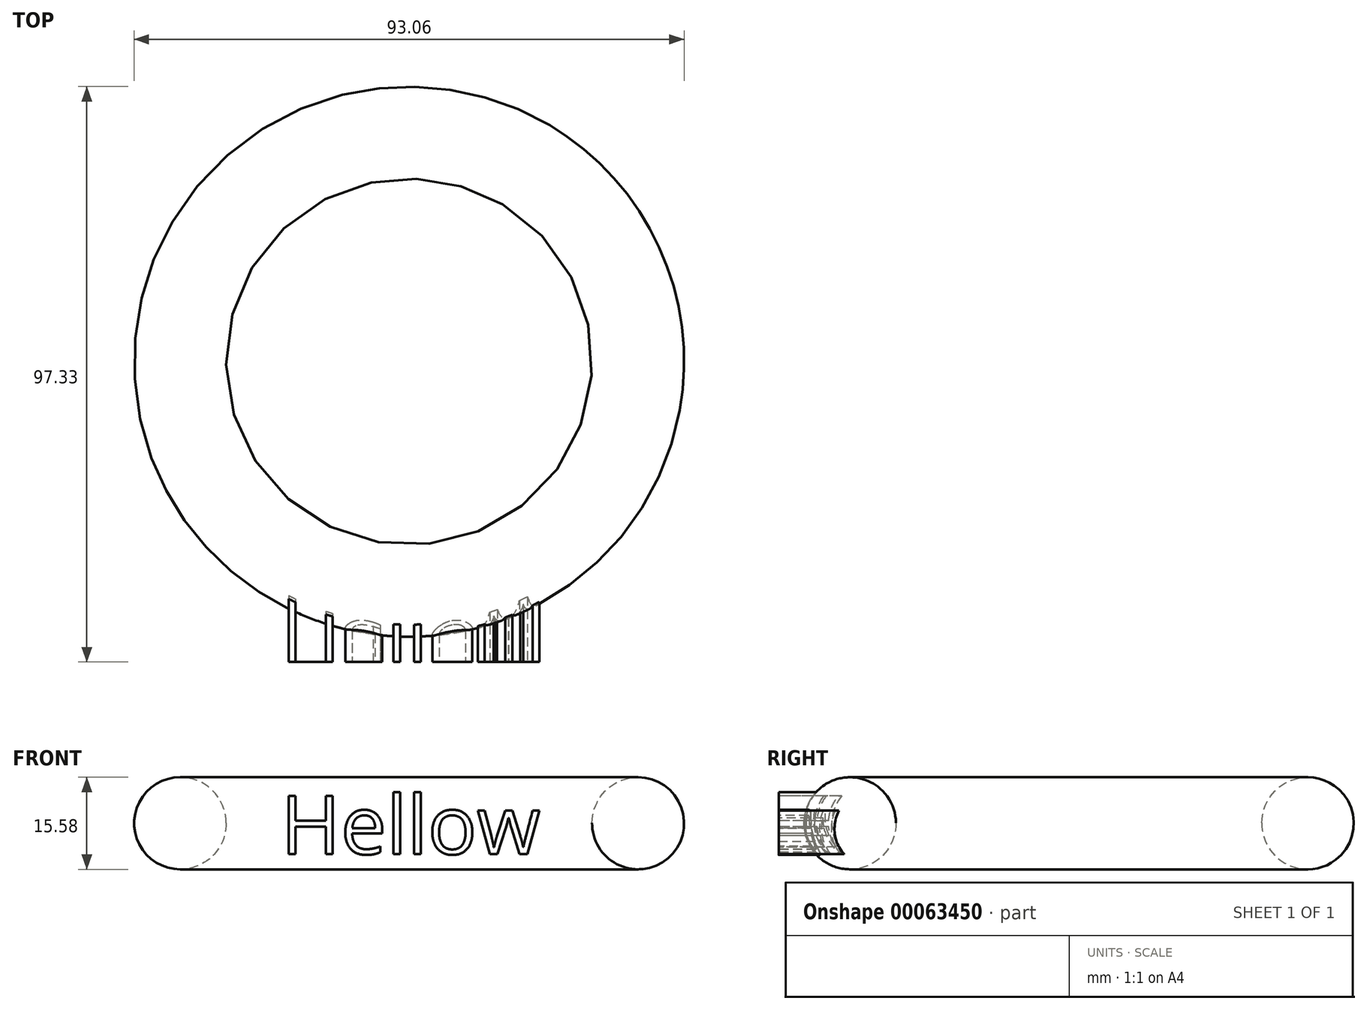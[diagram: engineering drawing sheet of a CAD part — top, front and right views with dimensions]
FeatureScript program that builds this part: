
annotation { "Feature Type Name" : "Feature", "Feature Type Description" : "" }
export const myFeature = defineFeature(function(context is Context, id is Id, definition is map)
    precondition{}
    {
        {
            var Q0;
            Q0=qCreatedBy(makeId("Front.planeOp"),FACE);
            var sketch = newSketch(context, id + "F0", { "sketchPlane" : qUnion([Q0])});
            skLineSegment(sketch, "E0", {"start": v(0, -42.07) * mm, "end": v(0, 42.06) * mm, "construction": true});
            skCircle(sketch, "E1", {"center": v(38.74, 0) * mm, "radius": 7.79 * mm});
            skSolve(sketch);
        }
        {
            var Q0;
            Q0=makeQuery(id+"F0.imprint","IMPRINT",FACE,{"disambiguationData":[TD([[makeQuery(id+"F0.imprint","IMPRINT",EDGE,{"derivedFrom":sQuery(id+"F0.wireOp",EDGE,"E1")}),1.0]])]});
            var Q1;
            Q1=sQuery(id+"F0.wireOp",EDGE,"E0");
            revolve(context, id + "F1", {"entities" : qUnion([Q0]), "axis" : qUnion([Q1]), "revolveType" : RevolveType.FULL});
        }
        {
            var Q0;
            Q0=qCreatedBy(makeId("Front.planeOp"),FACE);
            cPlane(context, id + "F2", {"entities" : qUnion([Q0]), "cplaneType" : CPlaneType.OFFSET, "offset" : 50.8 * mm, "width" : 152.4 * mm, "height" : 152.4 * mm});
        }
        {
            var Q0;
            Q0=qCreatedBy(id+"F2.planeOp",FACE);
            var sketch = newSketch(context, id + "F3", { "sketchPlane" : qUnion([Q0])});
            skText(sketch, "E2", { "text": "Hellow", "fontName": "OpenSans-Regular.ttf"});
            const initialGuessF3  = {"E2": [-0.02175, -0.00523, 1, 0, 0.00993]};
            skSetInitialGuess(sketch, initialGuessF3);
            skSolve(sketch);
        }
        {
            var Q0;
            Q0 = qSketchRegion(id + "F3", true);
            var Q1;
            Q1=makeQuery(id+"F1.opRevolve","SWEPT_BODY",BODY,{"disambiguationData":[OSD([sQuery(id+"F0.wireOp",EDGE,"E1")])]});
            extrude(context, id + "F4", {"entities" : qUnion([Q0]), "operationType" : NewBodyOperationType.ADD, "endBound" : BoundingType.UP_TO_BODY, "oppositeDirection" : true, "endBoundEntityBody" : qUnion([Q1]), "depth" : 25.4 * mm});
        }
    });
